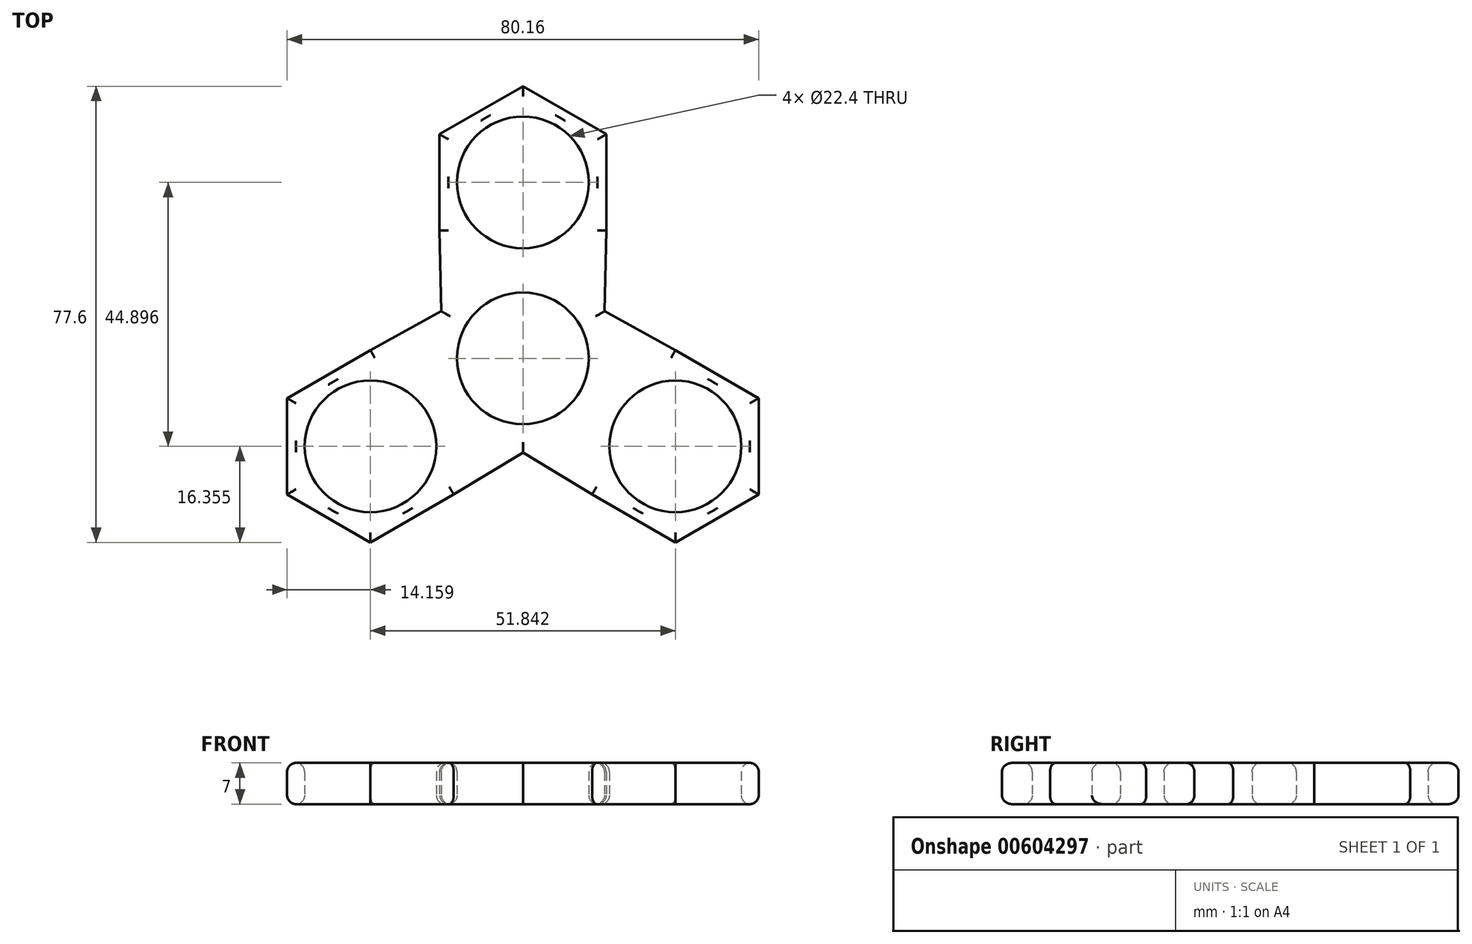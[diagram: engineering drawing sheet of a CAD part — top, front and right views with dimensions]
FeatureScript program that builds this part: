
annotation { "Feature Type Name" : "Feature", "Feature Type Description" : "" }
export const myFeature = defineFeature(function(context is Context, id is Id, definition is map)
    precondition{}
    {
        {
            var Q0;
            Q0=qCreatedBy(makeId("Top.planeOp"),FACE);
            var sketch = newSketch(context, id + "F0", { "sketchPlane" : qUnion([Q0])});
            skCircle(sketch, "E0", {"center": v(0, 0) * mm, "radius": 11.2 * mm});
            skArc(sketch, "E1.cCircle", {"start": v(-6.94, 12.01) * mm, "mid": v(-7.25, 11.82) * mm, "end": v(-7.57, 11.62) * mm, "construction": true});
            skLineSegment(sketch, "E1.2", {"start": v(-6.3, -12.38) * mm, "end": v(-6.94, -12.01) * mm});
            skLineSegment(sketch, "E1.4", {"start": v(-7.58, 11.64) * mm, "end": v(-6.94, 12.01) * mm});
            skPoint(sketch, "E1.0.midPoint", {"position": v(13.87, 0) * mm});
            skCircle(sketch, "E2", {"center": v(0, 29.93) * mm, "radius": 11.2 * mm});
            skLineSegment(sketch, "E3.0", {"start": v(14.16, 38.1) * mm, "end": v(14.16, 21.75) * mm});
            skLineSegment(sketch, "E3.2", {"start": v(0, 13.58) * mm, "end": v(-0.5, 13.86) * mm});
            skLineSegment(sketch, "E3.3", {"start": v(-14.16, 21.75) * mm, "end": v(-14.16, 38.1) * mm});
            skLineSegment(sketch, "E3.4", {"start": v(-14.16, 38.1) * mm, "end": v(0, 46.28) * mm});
            skLineSegment(sketch, "E3.5", {"start": v(0, 46.28) * mm, "end": v(14.16, 38.1) * mm});
            skPoint(sketch, "E3.0.midPoint", {"position": v(14.16, 29.93) * mm});
            skLineSegment(sketch, "E4.1.0", {"start": v(40.08, -6.79) * mm, "end": v(40.08, -23.14) * mm});
            skLineSegment(sketch, "E4.1.1", {"start": v(40.08, -23.14) * mm, "end": v(25.92, -31.32) * mm});
            skCircle(sketch, "E4.1.3", {"center": v(25.92, -14.97) * mm, "radius": 11.2 * mm});
            skPoint(sketch, "E4.1.5", {"position": v(18.84, -27.23) * mm});
            skLineSegment(sketch, "E4.1.7", {"start": v(25.92, -31.32) * mm, "end": v(11.76, -23.14) * mm});
            skLineSegment(sketch, "E4.1.8", {"start": v(25.92, 1.39) * mm, "end": v(40.08, -6.79) * mm});
            skLineSegment(sketch, "E4.2.0", {"start": v(-25.92, -31.32) * mm, "end": v(-40.08, -23.14) * mm});
            skLineSegment(sketch, "E4.2.1", {"start": v(-40.08, -23.14) * mm, "end": v(-40.08, -6.79) * mm});
            skCircle(sketch, "E4.2.3", {"center": v(-25.92, -14.97) * mm, "radius": 11.2 * mm});
            skPoint(sketch, "E4.2.5", {"position": v(-33, -2.7) * mm});
            skLineSegment(sketch, "E4.2.7", {"start": v(-40.08, -6.79) * mm, "end": v(-25.92, 1.39) * mm});
            skLineSegment(sketch, "E4.2.8", {"start": v(-11.76, -23.14) * mm, "end": v(-25.92, -31.32) * mm});
            skLineSegment(sketch, "E4.anchor1", {"start": v(-6.11, 9.39) * mm, "end": v(-7.57, 11.62) * mm, "construction": true});
            skLineSegment(sketch, "E4.anchor2", {"start": v(-5.07, -9.98) * mm, "end": v(-6.3, -12.38) * mm, "construction": true});
            skLineSegment(sketch, "E5", {"start": v(14.16, 21.75) * mm, "end": v(13.87, 8) * mm});
            skLineSegment(sketch, "E6", {"start": v(13.87, 8) * mm, "end": v(25.92, 1.39) * mm});
            skLineSegment(sketch, "E7", {"start": v(-14.16, 21.75) * mm, "end": v(-13.87, 8) * mm});
            skLineSegment(sketch, "E8", {"start": v(-25.92, 1.39) * mm, "end": v(-13.87, 8) * mm});
            skLineSegment(sketch, "E9", {"start": v(-11.76, -23.14) * mm, "end": v(0, -16.02) * mm});
            skLineSegment(sketch, "E10", {"start": v(0, -16.02) * mm, "end": v(11.76, -23.14) * mm});
            skLineSegment(sketch, "E11.trimOffspring", {"start": v(0.5, 13.86) * mm, "end": v(0, 13.58) * mm});
            skLineSegment(sketch, "E12.trimOffspring", {"start": v(-0.42, 15.77) * mm, "end": v(0, 16.02) * mm});
            skArc(sketch, "E13.trimOffspring", {"start": v(0.5, 13.86) * mm, "mid": v(0, 13.87) * mm, "end": v(-0.5, 13.86) * mm, "construction": true});
            skArc(sketch, "E14.trimOffspring", {"start": v(-6.94, -12.01) * mm, "mid": v(-6.61, -12.2) * mm, "end": v(-6.28, -12.37) * mm, "construction": true});
            skPoint(sketch, "E1.1.start.orphan", {"position": v(13.87, -8) * mm});
            skSolve(sketch);
        }
        {
            var Q0;
            Q0=makeQuery(id+"F0.imprint","IMPRINT",FACE,{"disambiguationData":[TD([[makeQuery(id+"F0.imprint","IMPRINT",EDGE,{"derivedFrom":sQuery(id+"F0.wireOp",EDGE,"E0")}),-1.0]])]});
            extrude(context, id + "F1", {"entities" : qUnion([Q0]), "depth" : 7 * mm, "offsetDistance" : 25 * mm});
        }
        {
            var Q0;
            Q0=makeQuery(id+"F1.opExtrude","CAP_FACE",FACE,{"disambiguationData":[OSD([sQuery(id+"F0.wireOp",EDGE,"E0"),sQuery(id+"F0.wireOp",EDGE,"E2"),sQuery(id+"F0.wireOp",EDGE,"E3.0"),sQuery(id+"F0.wireOp",EDGE,"E3.3"),sQuery(id+"F0.wireOp",EDGE,"E3.4"),sQuery(id+"F0.wireOp",EDGE,"E3.5"),sQuery(id+"F0.wireOp",EDGE,"E4.1.0"),sQuery(id+"F0.wireOp",EDGE,"E4.1.1"),sQuery(id+"F0.wireOp",EDGE,"E4.1.3"),sQuery(id+"F0.wireOp",EDGE,"E4.1.7"),sQuery(id+"F0.wireOp",EDGE,"E4.1.8"),sQuery(id+"F0.wireOp",EDGE,"E4.2.0"),sQuery(id+"F0.wireOp",EDGE,"E4.2.1"),sQuery(id+"F0.wireOp",EDGE,"E4.2.3"),sQuery(id+"F0.wireOp",EDGE,"E4.2.7"),sQuery(id+"F0.wireOp",EDGE,"E4.2.8"),sQuery(id+"F0.wireOp",EDGE,"E5"),sQuery(id+"F0.wireOp",EDGE,"E6"),sQuery(id+"F0.wireOp",EDGE,"E7"),sQuery(id+"F0.wireOp",EDGE,"E8"),sQuery(id+"F0.wireOp",EDGE,"E9"),sQuery(id+"F0.wireOp",EDGE,"E10")])],"isStart":false});
            fillet(context, id + "F2", {"entities" : qUnion([Q0]), "radius" : 1.5 * mm, "tangentPropagation" : true, "allowEdgeOverflow" : false});
        }
        {
            var Q0;
            Q0=makeQuery(id+"F1.opExtrude","CAP_FACE",FACE,{"disambiguationData":[OSD([sQuery(id+"F0.wireOp",EDGE,"E0"),sQuery(id+"F0.wireOp",EDGE,"E2"),sQuery(id+"F0.wireOp",EDGE,"E3.0"),sQuery(id+"F0.wireOp",EDGE,"E3.3"),sQuery(id+"F0.wireOp",EDGE,"E3.4"),sQuery(id+"F0.wireOp",EDGE,"E3.5"),sQuery(id+"F0.wireOp",EDGE,"E4.1.0"),sQuery(id+"F0.wireOp",EDGE,"E4.1.1"),sQuery(id+"F0.wireOp",EDGE,"E4.1.3"),sQuery(id+"F0.wireOp",EDGE,"E4.1.7"),sQuery(id+"F0.wireOp",EDGE,"E4.1.8"),sQuery(id+"F0.wireOp",EDGE,"E4.2.0"),sQuery(id+"F0.wireOp",EDGE,"E4.2.1"),sQuery(id+"F0.wireOp",EDGE,"E4.2.3"),sQuery(id+"F0.wireOp",EDGE,"E4.2.7"),sQuery(id+"F0.wireOp",EDGE,"E4.2.8"),sQuery(id+"F0.wireOp",EDGE,"E5"),sQuery(id+"F0.wireOp",EDGE,"E6"),sQuery(id+"F0.wireOp",EDGE,"E7"),sQuery(id+"F0.wireOp",EDGE,"E8"),sQuery(id+"F0.wireOp",EDGE,"E9"),sQuery(id+"F0.wireOp",EDGE,"E10")])],"isStart":true});
            fillet(context, id + "F3", {"entities" : qUnion([Q0]), "radius" : 1.5 * mm, "tangentPropagation" : true, "allowEdgeOverflow" : false});
        }
    });
